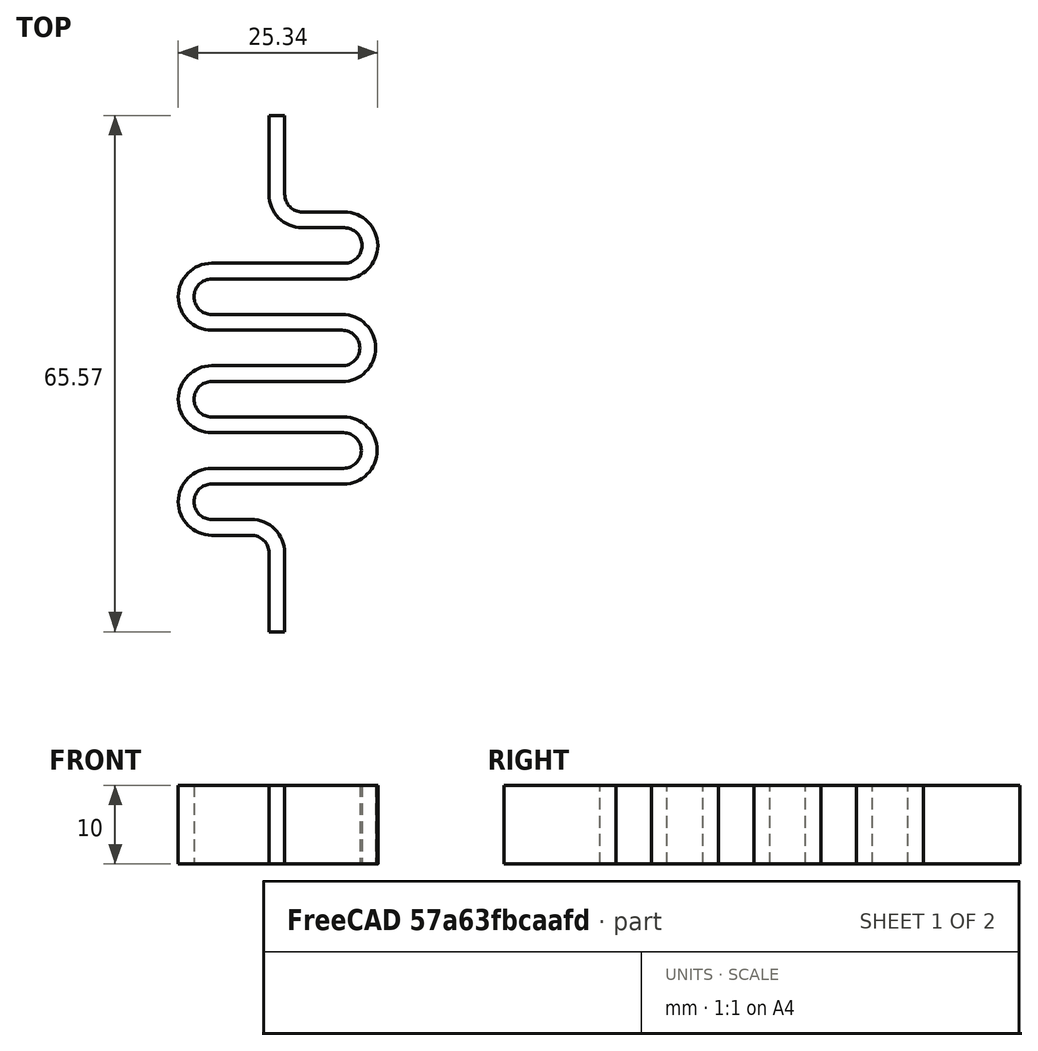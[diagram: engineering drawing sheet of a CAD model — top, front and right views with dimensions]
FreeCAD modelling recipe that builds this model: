
FCSTD DOCUMENT  (FreeCAD 0.19R23756 (Git))
Label: Feder1
License: All rights reserved
LicenseURL: http://en.wikipedia.org/wiki/All_rights_reserved
objects: Sketcher::SketchObject×1, PartDesign::Pad×1, PartDesign::Body×1, Fem::FemSolverObjectPython×1, App::MaterialObjectPython×1, Fem::ConstraintFixed×1, Fem::FemMeshShapeNetgenObject×1, Fem::ConstraintDisplacement×1, Fem::FemAnalysis×1
note: 4 computed .brp shape members not serialized (recipe doc carries the construction recipe); baked Part::Feature solids carry a one-line shape summary decoded from their .brp

FEATURE [Sketcher::SketchObject] Sketch
  FullyConstrained = false
  MapMode = 5
  Support = -> [XY_Plane]
  sketch-geometry (36):
    g0: ArcOfCircle CenterX=-8.26826 CenterY=19.8323 CenterZ=0 NormalX=0 NormalY=0 NormalZ=1 AngleXU=0 Radius=4.25498 StartAngle=1.5708 EndAngle=4.71239
    g1: ArcOfCircle CenterX=8.47209 CenterY=13.3223 CenterZ=0 NormalX=0 NormalY=0 NormalZ=1 AngleXU=0 Radius=4.25498 StartAngle=4.71239 EndAngle=7.85398
    g2: ArcOfCircle CenterX=-8.26826 CenterY=19.8323 CenterZ=0 NormalX=0 NormalY=0 NormalZ=1 AngleXU=0 Radius=2.25498 StartAngle=1.5708 EndAngle=4.71239
    g3: ArcOfCircle CenterX=8.47209 CenterY=13.3223 CenterZ=0 NormalX=0 NormalY=0 NormalZ=1 AngleXU=0 Radius=2.25498 StartAngle=4.71239 EndAngle=7.85398
    g4: LineSegment StartX=-8.26826 StartY=17.5773 StartZ=0 EndX=8.47209 EndY=17.5773 EndZ=0
    g5: LineSegment StartX=8.47209 StartY=15.5773 StartZ=0 EndX=-8.26826 EndY=15.5773 EndZ=0
    g6: LineSegment StartX=-8.26826 StartY=22.0873 StartZ=0 EndX=8.28692 EndY=22.0873 EndZ=0
    g7: LineSegment StartX=-8.26826 StartY=24.0873 StartZ=0 EndX=8.28692 EndY=24.0873 EndZ=0
    g8: ArcOfCircle CenterX=-8.26826 CenterY=32.8522 CenterZ=0 NormalX=0 NormalY=0 NormalZ=1 AngleXU=0 Radius=4.25498 StartAngle=1.5708 EndAngle=4.71239
    g9: ArcOfCircle CenterX=8.28692 CenterY=26.3423 CenterZ=0 NormalX=0 NormalY=0 NormalZ=1 AngleXU=0 Radius=4.25498 StartAngle=4.71239 EndAngle=7.85398
    g10: ArcOfCircle CenterX=-8.26826 CenterY=32.8522 CenterZ=0 NormalX=0 NormalY=0 NormalZ=1 AngleXU=0 Radius=2.25498 StartAngle=1.5708 EndAngle=4.71239
    g11: ArcOfCircle CenterX=8.28692 CenterY=26.3423 CenterZ=0 NormalX=0 NormalY=0 NormalZ=1 AngleXU=0 Radius=2.25498 StartAngle=4.71239 EndAngle=7.85398
    g12: LineSegment StartX=-8.26826 StartY=30.5972 StartZ=0 EndX=8.28692 EndY=30.5972 EndZ=0
    g13: LineSegment StartX=8.28692 StartY=28.5972 StartZ=0 EndX=-8.26826 EndY=28.5972 EndZ=0
    g14: LineSegment StartX=-8.26826 StartY=35.1072 StartZ=0 EndX=8.56853 EndY=35.1072 EndZ=0
    g15: LineSegment StartX=-8.26826 StartY=37.1072 StartZ=0 EndX=8.56853 EndY=37.1072 EndZ=0
    g16: ArcOfCircle CenterX=8.56853 CenterY=39.3622 CenterZ=0 NormalX=0 NormalY=0 NormalZ=1 AngleXU=0 Radius=2.25498 StartAngle=4.71239 EndAngle=7.85398
    g17: ArcOfCircle CenterX=8.56853 CenterY=39.3622 CenterZ=0 NormalX=0 NormalY=0 NormalZ=1 AngleXU=0 Radius=4.25498 StartAngle=4.71239 EndAngle=7.85398
    g18: LineSegment StartX=8.56853 StartY=41.6171 StartZ=0 EndX=3.25498 EndY=41.6171 EndZ=0
    g19: LineSegment StartX=8.56853 StartY=43.6171 StartZ=0 EndX=3.25498 EndY=43.6171 EndZ=0
    g20: ArcOfCircle CenterX=3.25498 CenterY=45.8721 CenterZ=0 NormalX=0 NormalY=0 NormalZ=1 AngleXU=0 Radius=4.25498 StartAngle=3.14159 EndAngle=4.71239
    g21: ArcOfCircle CenterX=3.25498 CenterY=45.8721 CenterZ=0 NormalX=0 NormalY=0 NormalZ=1 AngleXU=0 Radius=2.25498 StartAngle=3.14159 EndAngle=4.71239
    g22: LineSegment StartX=-8.26826 StartY=11.0674 StartZ=0 EndX=8.47209 EndY=11.0674 EndZ=0
    g23: LineSegment StartX=-8.26826 StartY=9.06737 StartZ=0 EndX=8.47209 EndY=9.06737 EndZ=0
    g24: ArcOfCircle CenterX=-8.26826 CenterY=6.81239 CenterZ=0 NormalX=0 NormalY=0 NormalZ=1 AngleXU=0 Radius=2.25498 StartAngle=1.5708 EndAngle=4.71239
    g25: ArcOfCircle CenterX=-8.26826 CenterY=6.81239 CenterZ=0 NormalX=0 NormalY=0 NormalZ=1 AngleXU=0 Radius=4.25498 StartAngle=1.5708 EndAngle=4.71239
    g26: LineSegment StartX=-3.25498 StartY=2.55741 StartZ=0 EndX=-8.26826 EndY=2.55741 EndZ=0
    g27: LineSegment StartX=-8.26826 StartY=4.55741 StartZ=0 EndX=-3.25498 EndY=4.55741 EndZ=0
    g28: ArcOfCircle CenterX=-3.25498 CenterY=0.302437 CenterZ=0 NormalX=0 NormalY=0 NormalZ=1 AngleXU=0 Radius=4.25498 StartAngle=0 EndAngle=1.5708
    g29: ArcOfCircle CenterX=-3.25498 CenterY=0.302437 CenterZ=0 NormalX=0 NormalY=0 NormalZ=1 AngleXU=0 Radius=2.25498 StartAngle=0 EndAngle=1.5708
    g30: LineSegment StartX=1 StartY=0.302437 StartZ=0 EndX=1 EndY=-9.69756 EndZ=0
    g31: LineSegment StartX=-1 StartY=0.302437 StartZ=0 EndX=-1 EndY=-9.69756 EndZ=0
    g32: LineSegment StartX=1 StartY=-9.69756 StartZ=0 EndX=-1 EndY=-9.69756 EndZ=0
    g33: LineSegment StartX=-1 StartY=45.8721 StartZ=0 EndX=-1 EndY=55.8721 EndZ=0
    g34: LineSegment StartX=-1 StartY=55.8721 StartZ=0 EndX=1 EndY=55.8721 EndZ=0
    g35: LineSegment StartX=1 StartY=55.8721 StartZ=0 EndX=1 EndY=45.8721 EndZ=0
  constraints (79):
    c: Tangent(g8,g15) = 1.5708
    c: Tangent(g10,g14) = 1.5708
    c: Tangent(g10,g12) = -1.5708
    c: Tangent(g8,g13) = 1.5708
    c: Tangent(g9,g12) = 1.5708
    c: Tangent(g11,g13) = -1.5708
    c: Tangent(g7,g11) = -1.5708
    c: Tangent(g6,g9) = -1.5708
    c: Tangent(g0,g7) = 1.5708
    c: Tangent(g2,g6) = 1.5708
    c: Tangent(g2,g4) = -1.5708
    c: Tangent(g0,g5) = 1.5708
    c: Tangent(g1,g4) = 1.5708
    c: Tangent(g3,g5) = -1.5708
    c: Coincident(g0,g2)
    c: Coincident(g8,g10)
    c: Coincident(g9,g11)
    c: Coincident(g1,g3)
    c: Vertical(g0,g0)
    c: Vertical(g0,g0)
    c: Vertical(g0,g2)
    c: Vertical(g2,g2)
    c: Vertical(g7,g8)
    c: Vertical(g8,g8)
    c: Vertical(g8,g8)
    c: Vertical(g8,g10)
    c: Vertical(g10,g10)
    c: Vertical(g1,g1)
    c: Vertical(g1,g3)
    c: Equal(g3,g2)
    c: Equal(g2,g11)
    c: Equal(g11,g10)
    c: Coincident(g17,g16)
    c: Vertical(g17,g17)
    c: Tangent(g15,g16) = -1.5708
    c: Tangent(g14,g17) = -1.5708
    c: Horizontal(g18)
    c: Coincident(g21,g20)
    c: Tangent(g21,g19) = 1.5708
    c: Tangent(g19,g17) = -1.5708
    c: Horizontal(g21,g20)
    c: Tangent(g20,g18) = 1.5708
    c: Tangent(g18,g16) = -1.5708
    c: Equal(g11,g16)
    c: Symmetric(g20,g21,g-2)
    c: Tangent(g25,g22) = 1.5708
    c: Tangent(g24,g23) = 1.5708
    c: Tangent(g24,g27) = -1.5708
    c: Tangent(g25,g26) = 1.5708
    c: Coincident(g25,g24)
    c: Vertical(g25,g25)
    c: Vertical(g24,g24)
    c: Tangent(g3,g22) = -1.5708
    c: Tangent(g1,g23) = -1.5708
    c: Vertical(g0,g24)
    c: Equal(g2,g24)
    c: Coincident(g29,g28)
    c: Tangent(g29,g26) = -1.5708
    c: Tangent(g28,g27) = 1.5708
    c: Symmetric(g28,g29,g-2)
    c: Horizontal(g28,g29)
    c: Coincident(g30,g28)
    c: Vertical(g30)
    c: Coincident(g31,g29)
    c: Vertical(g31)
    c: Coincident(g32,g30)
    c: Coincident(g32,g31)
    c: Horizontal(g32)
    c: DistanceX(g31,g30) = 2
    c: DistanceY(g30,g28) = 10
    c: Tangent(g20,g33) = 1.5708
    c: Coincident(g33,g34)
    c: Horizontal(g34)
    c: Coincident(g34,g35)
    c: Coincident(g35,g21)
    c: Vertical(g35)
    c: DistanceY(g20,g33) = 10
    c: Equal(g21,g29)
    c: Equal(g16,g21)
FEATURE [PartDesign::Pad] Pad
  Direction = (1,1,1)
  Length = 10
  Length2 = 100
  Profile = -> Sketch
  Type = 0
FEATURE [PartDesign::Body] Body
  Group = -> [Sketch,Pad]
  Origin = -> Origin
  Tip = -> Pad
FEATURE [Fem::FemSolverObjectPython] SolverCcxTools  # FEM object (typed FeaturePython)
  AnalysisType = 0
  BeamShellResultOutput3D = false
  EigenmodeHighLimit = 1000000
  EigenmodeLowLimit = 0
  EigenmodesCount = 10
  GeometricalNonlinearity = 0
  IterationsControlParameterCutb = 0.25,0.5,0.75,0.85,,,1.5,
  IterationsControlParameterIter = 4,8,9,200,10,400,,200,,
  IterationsControlParameterTimeUse = false
  IterationsThermoMechMaximum = 2000
  IterationsUserDefinedIncrementations = false
  IterationsUserDefinedTimeStepLength = false
  MaterialNonlinearity = 0
  MatrixSolverType = 0
  SplitInputWriter = false
  ThermoMechSteadyState = true
  TimeEnd = 1
  TimeInitialStep = 0.01
FEATURE [App::MaterialObjectPython] MaterialSolid  # material (typed FeaturePython)
  Category = 0
  Material = AuthorAndLicense=PLA-Generic,CardName=PLA-Generic,Density=1240 kg/m^3,+12 more (map truncated)
FEATURE [Fem::ConstraintFixed] ConstraintFixed
  NormalDirection = (0,1,0)
  Normals = (9) [(0,1,0),(0,1,0),(0,1,0),(0,1,0),(0,1,0),(0,1,0),(0,1,0),(0,1,0),(0,1,0)]
  Points = (9) [(-1,55.8721,10),(5.55112e-16,55.8721,10),(1,55.8721,10),(-1,55.8721,5),(5.55112e-16,55.8721,5),(1,55.8721,5),(-1,55.8721,0),(5.55112e-16,55.8721,0),(1,55.8721,0)]
  References = -> [Pad]
FEATURE [Fem::FemMeshShapeNetgenObject] FEMMeshNetgen
  Fineness = 2
  GrowthRate = 0.3
  MaxSize = 1000
  NbSegsPerEdge = 1
  NbSegsPerRadius = 2
  Optimize = true
  SecondOrder = true
  Shape = -> Pad
FEATURE [Fem::ConstraintDisplacement] ConstraintDisplacement
  NormalDirection = (0,-1,0)
  Normals = (9) [(0,-1,0),(0,-1,0),(0,-1,0),(0,-1,0),(0,-1,0),(0,-1,0),(0,-1,0),(0,-1,0),(0,-1,0)]
  Points = (9) [(1,-9.69756,10),(0,-9.69756,10),(-1,-9.69756,10),(1,-9.69756,5),(0,-9.69756,5),(-1,-9.69756,5),(1,-9.69756,0),(0,-9.69756,0),(-1,-9.69756,0)]
  References = -> [Pad]
  rotxFix = false
  rotxFree = true
  rotyFix = false
  rotyFree = true
  rotzFix = false
  rotzFree = true
  xDisplacement = 0
  xFix = false
  xFree = true
  xRotation = 0
  yDisplacement = -20
  yFix = false
  yFree = false
  yRotation = 0
  zDisplacement = 0
  zFix = false
  zFree = true
  zRotation = 0
FEATURE [Fem::FemAnalysis] Analysis
  Group = -> [SolverCcxTools,MaterialSolid,ConstraintFixed,FEMMeshNetgen,ConstraintDisplacement]
